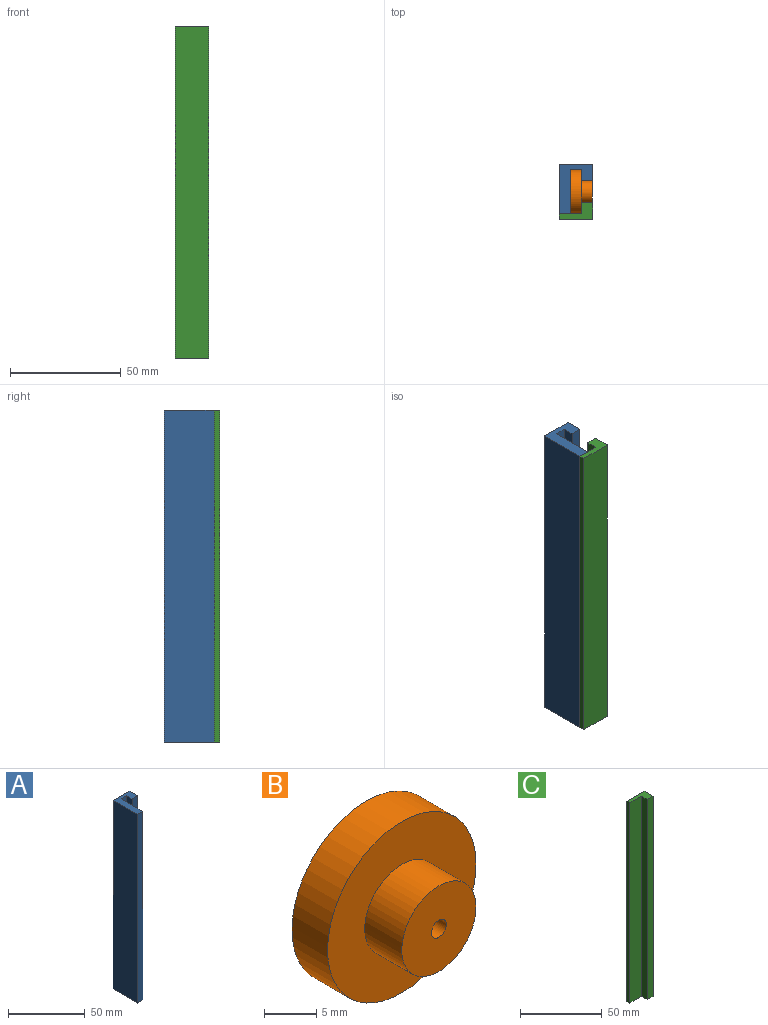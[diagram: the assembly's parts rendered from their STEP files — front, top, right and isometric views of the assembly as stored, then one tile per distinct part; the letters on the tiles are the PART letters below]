
ASSEMBLY  parts=3 mates=2
PART A: 10 faces, bbox 15x22.5x150 mm
  f0: plane 150x5mm, normal (0,-1,0), area 750mm2, adj f2,f4,f6,f8
  f1: plane 150x22.5mm, normal (-1,0,0), area 3375mm2, adj f2,f4,f5,f7
  f2: plane 22.5x15mm, normal (0,0,-1), area 162.5mm2, adj f0,f1,f3,f5,f6,f7,f8,f9
  f3: plane 150x7.5mm, normal (1,0,0), area 1125mm2, adj f2,f4,f5,f9
  f4: plane 22.5x15mm, normal (0,0,1), area 162.5mm2, adj f0,f1,f3,f5,f6,f7,f8,f9
  f5: plane 150x15mm, normal (0,1,0), area 2250mm2, adj f1,f2,f3,f4
  f6: plane 150x20mm, normal (1,0,0), area 3000mm2, adj f0,f2,f4,f7
  f7: plane 150x5mm, normal (0,-1,0), area 750mm2, adj f1,f2,f4,f6
  f8: plane 150x5mm, normal (-1,0,0), area 750mm2, adj f0,f2,f4,f9
  f9: plane 150x5mm, normal (0,-1,0), area 750mm2, adj f2,f3,f4,f8
PART B: 6 faces, bbox 20x9.8x20 mm
  f0: cylinder r=1mm len=9.8mm, axis (0,1,0), area 61.6mm2, adj f3,f5
  f1: cylinder r=10mm len=20mm, axis (0,1,0), area 301.6mm2, adj f2,f3
  f2: plane 20x20mm, normal (0,-1,0), area 235.6mm2, adj f1,f4
  f3: plane 20x20mm, normal (0,1,0), area 311mm2, adj f0,f1
  f4: cylinder r=5mm len=10mm, axis (0,1,0), area 157.1mm2, adj f2,f5
  f5: plane 10x10mm, normal (0,-1,0), area 75.4mm2, adj f0,f4
PART C: 8 faces, bbox 15x7.5x150 mm
  f0: plane 150x10mm, normal (0,-1,0), area 1500mm2, adj f1,f2,f4,f6
  f1: plane 150x2.5mm, normal (-1,0,0), area 375mm2, adj f0,f2,f4,f5
  f2: plane 15x7.5mm, normal (0,0,-1), area 62.5mm2, adj f0,f1,f3,f5,f6,f7
  f3: plane 150x7.5mm, normal (1,0,0), area 1125mm2, adj f2,f4,f5,f7
  f4: plane 15x7.5mm, normal (0,0,1), area 62.5mm2, adj f0,f1,f3,f5,f6,f7
  f5: plane 150x15mm, normal (0,1,0), area 2250mm2, adj f1,f2,f3,f4
  f6: plane 150x5mm, normal (-1,0,0), area 750mm2, adj f0,f2,f4,f7
  f7: plane 150x5mm, normal (0,-1,0), area 750mm2, adj f2,f3,f4,f6
PLACE A t=(-68.33,11.35,-22.18)mm
PLACE B rot(axis=(-0.58,0.58,0.58),120deg) t=(-63.33,-13.36,10.87)mm
PLACE C rot(axis=(1,0,0),180deg) t=(-92.75,-13.65,127.82)mm
MATE fastened C.f0 <-> A.f7  axis (0,1,0) through (-68.33,-11.15,52.82)mm
MATE fastened B.f0 <-> A.f6  axis (-1,0,0) through (-63.33,-1.15,52.82)mm
